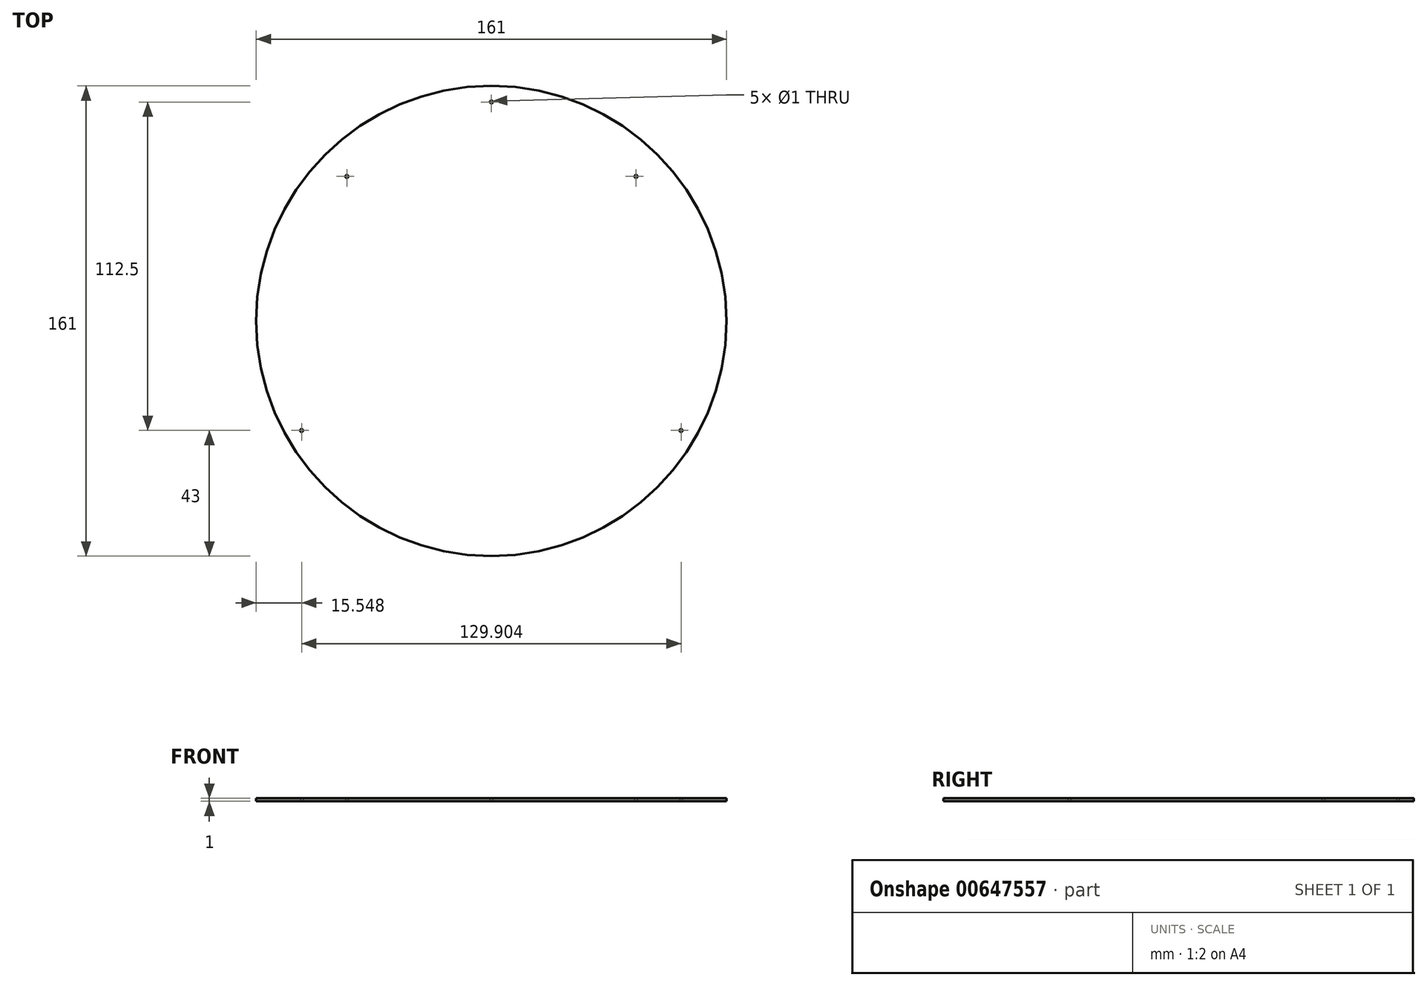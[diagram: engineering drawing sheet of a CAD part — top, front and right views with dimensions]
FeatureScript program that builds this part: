
annotation { "Feature Type Name" : "Feature", "Feature Type Description" : "" }
export const myFeature = defineFeature(function(context is Context, id is Id, definition is map)
    precondition{}
    {
        {
            var Q0;
            Q0=qCreatedBy(makeId("Top.planeOp"),FACE);
            var sketch = newSketch(context, id + "F0", { "sketchPlane" : qUnion([Q0])});
            skLineSegment(sketch, "E0", {"start": v(0, 75) * mm, "end": v(0, 0) * mm});
            skLineSegment(sketch, "E1", {"start": v(64.95, -37.5) * mm, "end": v(0, 0) * mm});
            skLineSegment(sketch, "E2", {"start": v(-49.48, 49.5) * mm, "end": v(49.52, 49.5) * mm});
            skLineSegment(sketch, "E3", {"start": v(0, 0) * mm, "end": v(-64.95, -37.5) * mm});
            skLineSegment(sketch, "E4", {"start": v(-64.95, -37.5) * mm, "end": v(64.95, -37.5) * mm});
            skCircle(sketch, "E5", {"center": v(0, 0) * mm, "radius": 80.5 * mm});
            skSolve(sketch);
        }
        {
            var Q0;
            Q0=makeQuery(id+"F0.imprint","IMPRINT",FACE,{"disambiguationData":[TD([[makeQuery(id+"F0.imprint","IMPRINT",EDGE,{"derivedFrom":sQuery(id+"F0.wireOp",EDGE,"E1")}),1.0]])]});
            var Q1;
            Q1=makeQuery(id+"F0.imprint","IMPRINT",FACE,{"disambiguationData":[TD([[makeQuery(id+"F0.imprint","IMPRINT",EDGE,{"derivedFrom":sQuery(id+"F0.wireOp",EDGE,"E1")}),-1.0]])]});
            extrude(context, id + "F1", {"entities" : qUnion([Q0, Q1]), "depth" : 1 * mm, "offsetDistance" : 25 * mm});
        }
        {
            var Q0;
            Q0=sQuery(id+"F0.wireOp",VERTEX,"E2.start");
            var Q1;
            Q1=sQuery(id+"F0.wireOp",VERTEX,"E2.end");
            var Q2;
            Q2=sQuery(id+"F0.wireOp",VERTEX,"E0.start");
            var Q3;
            Q3=sQuery(id+"F0.wireOp",VERTEX,"E3.end");
            var Q4;
            Q4=sQuery(id+"F0.wireOp",VERTEX,"E1.start");
            var Q5;
            Q5=makeQuery(id+"F1.opExtrude","SWEPT_BODY",BODY,{"disambiguationData":[OSD([sQuery(id+"F0.wireOp",EDGE,"E5")])]});
            hole(context, id + "F2", {"style" : HoleStyle.SIMPLE, "endStyle" : HoleEndStyle.BLIND, "oppositeDirection" : true, "holeDiameter" : 1 * mm, "majorDiameter" : 5 * mm, "holeDepth" : 7 * mm, "isTappedThrough" : true, "tappedDepth" : 12 * mm, "tapClearance" : 3, "startFromSketch" : true, "locations" : qUnion([Q0, Q1, Q2, Q3, Q4]), "scope" : qUnion([Q5])});
        }
    });
